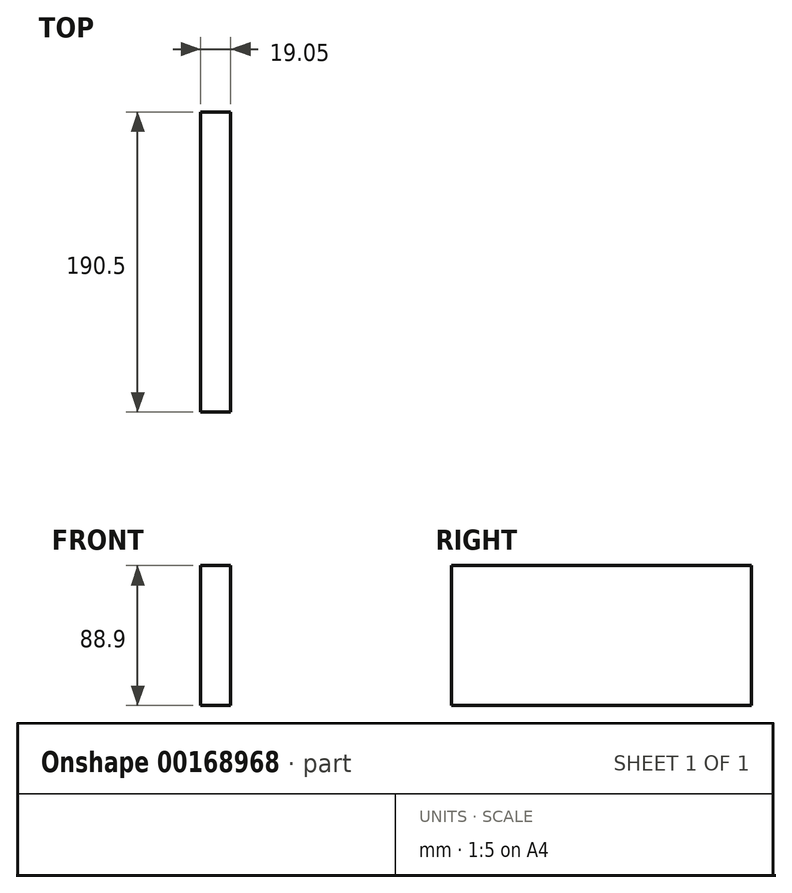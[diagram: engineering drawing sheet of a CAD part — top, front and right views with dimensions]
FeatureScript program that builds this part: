
annotation { "Feature Type Name" : "Feature", "Feature Type Description" : "" }
export const myFeature = defineFeature(function(context is Context, id is Id, definition is map)
    precondition{}
    {
        {
            var Q0;
            Q0=qCreatedBy(makeId("Right.planeOp"),FACE);
            var sketch = newSketch(context, id + "F0", { "sketchPlane" : qUnion([Q0])});
            skLineSegment(sketch, "E0.bottom", {"start": v(-21.15, 77.26) * mm, "end": v(169.35, 77.26) * mm});
            skLineSegment(sketch, "E0.top", {"start": v(-21.15, -11.64) * mm, "end": v(169.35, -11.64) * mm});
            skLineSegment(sketch, "E0.left", {"start": v(-21.15, 77.26) * mm, "end": v(-21.15, -11.64) * mm});
            skLineSegment(sketch, "E0.right", {"start": v(169.35, 77.26) * mm, "end": v(169.35, -11.64) * mm});
            skSolve(sketch);
        }
        {
            var Q0;
            Q0 = qSketchRegion(id + "F0", true);
            extrude(context, id + "F1", {"entities" : qUnion([Q0]), "depth" : 19.05 * mm});
        }
    });
